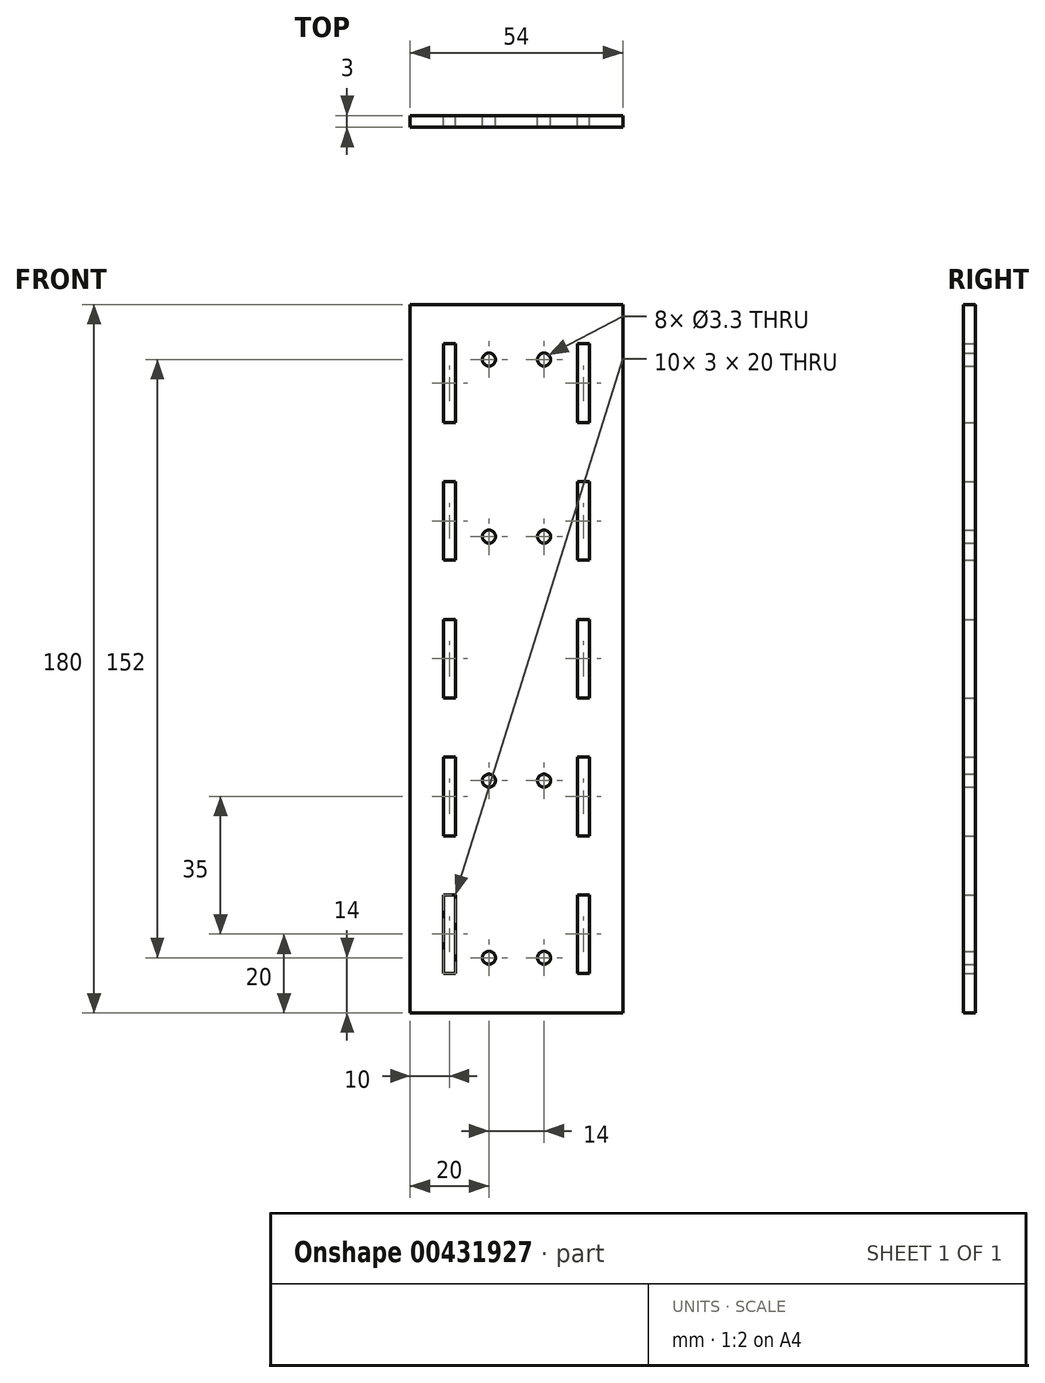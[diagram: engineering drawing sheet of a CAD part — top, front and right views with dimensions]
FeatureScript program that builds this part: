
annotation { "Feature Type Name" : "Feature", "Feature Type Description" : "" }
export const myFeature = defineFeature(function(context is Context, id is Id, definition is map)
    precondition{}
    {
        {
            var Q0;
            Q0=qCreatedBy(makeId("Front.planeOp"),FACE);
            var sketch = newSketch(context, id + "F0", { "sketchPlane" : qUnion([Q0])});
            skLineSegment(sketch, "E0.bottom", {"start": v(-27, 90) * mm, "end": v(27, 90) * mm});
            skLineSegment(sketch, "E0.top", {"start": v(-27, -90) * mm, "end": v(27, -90) * mm});
            skLineSegment(sketch, "E0.left", {"start": v(-27, 90) * mm, "end": v(-27, -90) * mm});
            skLineSegment(sketch, "E0.right", {"start": v(27, 90) * mm, "end": v(27, -90) * mm});
            skPoint(sketch, "E0.middle", {"position": v(0, 0) * mm});
            skCircle(sketch, "E1", {"center": v(-7, -31) * mm, "radius": 1.65 * mm});
            skCircle(sketch, "E2.0.1.0", {"center": v(-7, -76) * mm, "radius": 1.65 * mm});
            skCircle(sketch, "E2.1.0.0", {"center": v(7, -31) * mm, "radius": 1.65 * mm});
            skCircle(sketch, "E2.1.1.0", {"center": v(7, -76) * mm, "radius": 1.65 * mm});
            skLineSegment(sketch, "E2.direction1", {"start": v(-7, -31) * mm, "end": v(7, -31) * mm, "construction": true});
            skLineSegment(sketch, "E2.direction2", {"start": v(-7, -31) * mm, "end": v(-7, -76) * mm, "construction": true});
            skCircle(sketch, "E3", {"center": v(-7, 31) * mm, "radius": 1.65 * mm});
            skCircle(sketch, "E4.0.1.0", {"center": v(-7, 76) * mm, "radius": 1.65 * mm});
            skCircle(sketch, "E4.1.0.0", {"center": v(7, 31) * mm, "radius": 1.65 * mm});
            skCircle(sketch, "E4.1.1.0", {"center": v(7, 76) * mm, "radius": 1.65 * mm});
            skLineSegment(sketch, "E4.direction1", {"start": v(-7, 31) * mm, "end": v(7, 31) * mm, "construction": true});
            skLineSegment(sketch, "E4.direction2", {"start": v(-7, 31) * mm, "end": v(-7, 76) * mm, "construction": true});
            skLineSegment(sketch, "E5.bottom", {"start": v(-15.5, 10) * mm, "end": v(-18.5, 10) * mm});
            skLineSegment(sketch, "E5.top", {"start": v(-15.5, -10) * mm, "end": v(-18.5, -10) * mm});
            skLineSegment(sketch, "E5.left", {"start": v(-15.5, 10) * mm, "end": v(-15.5, -10) * mm});
            skLineSegment(sketch, "E5.right", {"start": v(-18.5, 10) * mm, "end": v(-18.5, -10) * mm});
            skPoint(sketch, "E5.middle", {"position": v(-17, 0) * mm});
            skLineSegment(sketch, "E6.0.1.0", {"start": v(-15.5, 25) * mm, "end": v(-18.5, 25) * mm});
            skLineSegment(sketch, "E6.0.1.1", {"start": v(-18.5, 45) * mm, "end": v(-18.5, 25) * mm});
            skPoint(sketch, "E6.0.1.2", {"position": v(-17, 35) * mm});
            skLineSegment(sketch, "E6.0.1.3", {"start": v(-15.5, 45) * mm, "end": v(-15.5, 25) * mm});
            skLineSegment(sketch, "E6.0.1.4", {"start": v(-15.5, 45) * mm, "end": v(-18.5, 45) * mm});
            skLineSegment(sketch, "E6.0.2.0", {"start": v(-15.5, 60) * mm, "end": v(-18.5, 60) * mm});
            skLineSegment(sketch, "E6.0.2.1", {"start": v(-18.5, 80) * mm, "end": v(-18.5, 60) * mm});
            skPoint(sketch, "E6.0.2.2", {"position": v(-17, 70) * mm});
            skLineSegment(sketch, "E6.0.2.3", {"start": v(-15.5, 80) * mm, "end": v(-15.5, 60) * mm});
            skLineSegment(sketch, "E6.0.2.4", {"start": v(-15.5, 80) * mm, "end": v(-18.5, 80) * mm});
            skLineSegment(sketch, "E6.1.0.0", {"start": v(18.5, -10) * mm, "end": v(15.5, -10) * mm});
            skLineSegment(sketch, "E6.1.0.1", {"start": v(15.5, 10) * mm, "end": v(15.5, -10) * mm});
            skPoint(sketch, "E6.1.0.2", {"position": v(17, 0) * mm});
            skLineSegment(sketch, "E6.1.0.3", {"start": v(18.5, 10) * mm, "end": v(18.5, -10) * mm});
            skLineSegment(sketch, "E6.1.0.4", {"start": v(18.5, 10) * mm, "end": v(15.5, 10) * mm});
            skLineSegment(sketch, "E6.1.1.0", {"start": v(18.5, 25) * mm, "end": v(15.5, 25) * mm});
            skLineSegment(sketch, "E6.1.1.1", {"start": v(15.5, 45) * mm, "end": v(15.5, 25) * mm});
            skPoint(sketch, "E6.1.1.2", {"position": v(17, 35) * mm});
            skLineSegment(sketch, "E6.1.1.3", {"start": v(18.5, 45) * mm, "end": v(18.5, 25) * mm});
            skLineSegment(sketch, "E6.1.1.4", {"start": v(18.5, 45) * mm, "end": v(15.5, 45) * mm});
            skLineSegment(sketch, "E6.1.2.0", {"start": v(18.5, 60) * mm, "end": v(15.5, 60) * mm});
            skLineSegment(sketch, "E6.1.2.1", {"start": v(15.5, 80) * mm, "end": v(15.5, 60) * mm});
            skPoint(sketch, "E6.1.2.2", {"position": v(17, 70) * mm});
            skLineSegment(sketch, "E6.1.2.3", {"start": v(18.5, 80) * mm, "end": v(18.5, 60) * mm});
            skLineSegment(sketch, "E6.1.2.4", {"start": v(18.5, 80) * mm, "end": v(15.5, 80) * mm});
            skLineSegment(sketch, "E6.direction1", {"start": v(-18.5, -10) * mm, "end": v(15.5, -10) * mm, "construction": true});
            skLineSegment(sketch, "E6.direction2", {"start": v(-18.5, -10) * mm, "end": v(-18.5, 25) * mm, "construction": true});
            skPoint(sketch, "E7.0.1.0", {"position": v(17, -35) * mm});
            skLineSegment(sketch, "E7.0.1.1", {"start": v(15.5, -25) * mm, "end": v(15.5, -45) * mm});
            skLineSegment(sketch, "E7.0.1.2", {"start": v(18.5, -45) * mm, "end": v(15.5, -45) * mm});
            skLineSegment(sketch, "E7.0.1.3", {"start": v(18.5, -25) * mm, "end": v(18.5, -45) * mm});
            skLineSegment(sketch, "E7.0.1.4", {"start": v(18.5, -25) * mm, "end": v(15.5, -25) * mm});
            skPoint(sketch, "E7.0.2.0", {"position": v(17, -70) * mm});
            skLineSegment(sketch, "E7.0.2.1", {"start": v(15.5, -60) * mm, "end": v(15.5, -80) * mm});
            skLineSegment(sketch, "E7.0.2.2", {"start": v(18.5, -80) * mm, "end": v(15.5, -80) * mm});
            skLineSegment(sketch, "E7.0.2.3", {"start": v(18.5, -60) * mm, "end": v(18.5, -80) * mm});
            skLineSegment(sketch, "E7.0.2.4", {"start": v(18.5, -60) * mm, "end": v(15.5, -60) * mm});
            skPoint(sketch, "E7.1.1.0", {"position": v(-17, -35) * mm});
            skLineSegment(sketch, "E7.1.1.1", {"start": v(-18.5, -25) * mm, "end": v(-18.5, -45) * mm});
            skLineSegment(sketch, "E7.1.1.2", {"start": v(-15.5, -45) * mm, "end": v(-18.5, -45) * mm});
            skLineSegment(sketch, "E7.1.1.3", {"start": v(-15.5, -25) * mm, "end": v(-15.5, -45) * mm});
            skLineSegment(sketch, "E7.1.1.4", {"start": v(-15.5, -25) * mm, "end": v(-18.5, -25) * mm});
            skPoint(sketch, "E7.1.2.0", {"position": v(-17, -70) * mm});
            skLineSegment(sketch, "E7.1.2.1", {"start": v(-18.5, -60) * mm, "end": v(-18.5, -80) * mm});
            skLineSegment(sketch, "E7.1.2.2", {"start": v(-15.5, -80) * mm, "end": v(-18.5, -80) * mm});
            skLineSegment(sketch, "E7.1.2.3", {"start": v(-15.5, -60) * mm, "end": v(-15.5, -80) * mm});
            skLineSegment(sketch, "E7.1.2.4", {"start": v(-15.5, -60) * mm, "end": v(-18.5, -60) * mm});
            skLineSegment(sketch, "E7.direction1", {"start": v(15.5, -10) * mm, "end": v(-18.5, -10) * mm, "construction": true});
            skLineSegment(sketch, "E7.direction2", {"start": v(15.5, -10) * mm, "end": v(15.5, -45) * mm, "construction": true});
            skSolve(sketch);
        }
        {
            var Q0;
            Q0=makeQuery(id+"F0.imprint","IMPRINT",FACE,{"disambiguationData":[TD([[makeQuery(id+"F0.imprint","IMPRINT",EDGE,{"derivedFrom":sQuery(id+"F0.wireOp",EDGE,"E0.bottom")}),-1.0]])]});
            extrude(context, id + "F1", {"entities" : qUnion([Q0]), "depth" : 3 * mm});
        }
    });
